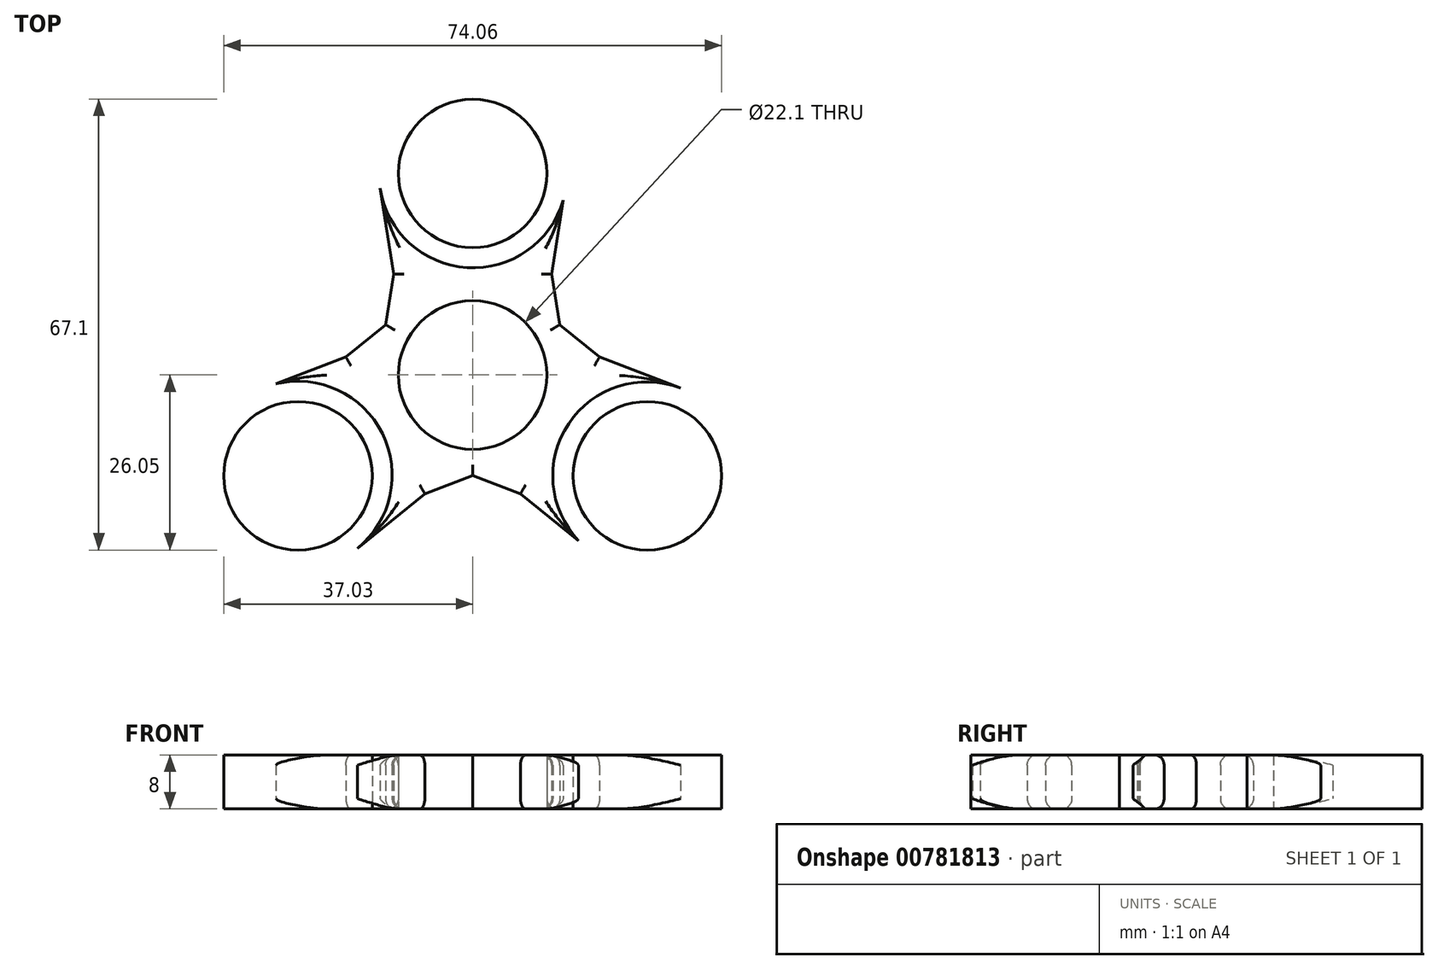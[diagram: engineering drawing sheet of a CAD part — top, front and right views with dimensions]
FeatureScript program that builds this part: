
annotation { "Feature Type Name" : "Feature", "Feature Type Description" : "" }
export const myFeature = defineFeature(function(context is Context, id is Id, definition is map)
    precondition{}
    {
        {
            var Q0;
            Q0=qCreatedBy(makeId("Top.planeOp"),FACE);
            var sketch = newSketch(context, id + "F0", { "sketchPlane" : qUnion([Q0])});
            skCircle(sketch, "E0", {"center": v(0, 0) * mm, "radius": 11.05 * mm});
            skCircle(sketch, "E1", {"center": v(0, 0) * mm, "radius": 14 * mm});
            skLineSegment(sketch, "E2", {"start": v(-20.51, 15) * mm, "end": v(20.51, 15) * mm, "construction": true});
            skLineSegment(sketch, "E3", {"start": v(0, 30) * mm, "end": v(0, 0) * mm, "construction": true});
            skSolve(sketch);
        }
        {
            var Q0;
            Q0=makeQuery(id+"F0.imprint","IMPRINT",FACE,{"disambiguationData":[TD([[makeQuery(id+"F0.imprint","IMPRINT",EDGE,{"derivedFrom":sQuery(id+"F0.wireOp",EDGE,"E0")}),-1.0]])]});
            extrude(context, id + "F1", {"entities" : qUnion([Q0]), "depth" : 8 * mm, "offsetDistance" : 25 * mm});
        }
        {
            var Q0;
            Q0=qCreatedBy(makeId("Top.planeOp"),FACE);
            var sketch = newSketch(context, id + "F2", { "sketchPlane" : qUnion([Q0])});
            skCircle(sketch, "E4.MirrorC", {"center": v(0.06, 29.96) * mm, "radius": 14 * mm});
            skCircle(sketch, "E5.MirrorC", {"center": v(0, 30) * mm, "radius": 11.05 * mm});
            skLineSegment(sketch, "E6.0", {"start": v(-20.51, 15) * mm, "end": v(20.51, 15) * mm, "construction": true});
            skLineSegment(sketch, "E7", {"start": v(-13.77, 27.77) * mm, "end": v(-11.75, 15) * mm});
            skCircle(sketch, "E8.0", {"center": v(0, 0) * mm, "radius": 14 * mm});
            skLineSegment(sketch, "E9", {"start": v(-11.75, 15) * mm, "end": v(-12.97, 7.49) * mm});
            skLineSegment(sketch, "E10.MirrorCS", {"start": v(13.77, 27.77) * mm, "end": v(11.75, 15) * mm});
            skLineSegment(sketch, "E11.MirrorCS", {"start": v(11.75, 15) * mm, "end": v(12.97, 7.49) * mm});
            skCircle(sketch, "E12.1.0", {"center": v(-25.98, -15) * mm, "radius": 11.05 * mm});
            skCircle(sketch, "E12.1.1", {"center": v(-25.97, -14.93) * mm, "radius": 14 * mm});
            skLineSegment(sketch, "E12.1.2", {"start": v(-17.16, -25.8) * mm, "end": v(-7.12, -17.67) * mm});
            skLineSegment(sketch, "E12.1.3", {"start": v(-7.12, -17.67) * mm, "end": v(0, -14.97) * mm});
            skLineSegment(sketch, "E12.1.4", {"start": v(-18.86, 2.67) * mm, "end": v(-12.97, 7.49) * mm});
            skLineSegment(sketch, "E12.1.5", {"start": v(-30.93, -1.96) * mm, "end": v(-18.86, 2.67) * mm});
            skCircle(sketch, "E12.2.0", {"center": v(25.98, -15) * mm, "radius": 11.05 * mm});
            skCircle(sketch, "E12.2.1", {"center": v(25.91, -15.03) * mm, "radius": 14 * mm});
            skLineSegment(sketch, "E12.2.2", {"start": v(30.93, -1.96) * mm, "end": v(18.86, 2.67) * mm});
            skLineSegment(sketch, "E12.2.3", {"start": v(18.86, 2.67) * mm, "end": v(12.97, 7.49) * mm});
            skLineSegment(sketch, "E12.2.4", {"start": v(7.12, -17.67) * mm, "end": v(0, -14.97) * mm});
            skLineSegment(sketch, "E12.2.5", {"start": v(17.16, -25.8) * mm, "end": v(7.12, -17.67) * mm});
            skPoint(sketch, "E13.orphan", {"position": v(-8.85, 10.84) * mm});
            skPoint(sketch, "E14.orphan", {"position": v(-13.82, 2.25) * mm});
            skPoint(sketch, "E15.orphan", {"position": v(4.96, -13.1) * mm});
            skPoint(sketch, "E16.orphan", {"position": v(-4.96, -13.1) * mm});
            skPoint(sketch, "E17.orphan", {"position": v(13.82, 2.25) * mm});
            skPoint(sketch, "E18.orphan", {"position": v(8.85, 10.84) * mm});
            skSolve(sketch);
        }
        {
            var Q0;
            Q0=makeQuery(id+"F2.imprint","IMPRINT",FACE,{"disambiguationData":[TD([[makeQuery(id+"F2.imprint","IMPRINT",EDGE,{"derivedFrom":sQuery(id+"F2.wireOp",EDGE,"E5.MirrorC")}),1.0]])]});
            var Q1;
            {var subQ9=sQuery(id+"F2.wireOp",EDGE,"E7");Q1=makeQuery(id+"F2.imprint","IMPRINT",FACE,{"disambiguationData":[TD([[makeQuery(id+"F2.imprint","IMPRINT",EDGE,{"derivedFrom":subQ9}),1.0]])]});}
            var Q2;
            Q2=makeQuery(id+"F2.imprint","IMPRINT",FACE,{"disambiguationData":[TD([[makeQuery(id+"F2.imprint","IMPRINT",EDGE,{"derivedFrom":sQuery(id+"F2.wireOp",EDGE,"E12.1.0")}),1.0]])]});
            var Q3;
            Q3=makeQuery(id+"F2.imprint","IMPRINT",FACE,{"disambiguationData":[TD([[makeQuery(id+"F2.imprint","IMPRINT",EDGE,{"derivedFrom":sQuery(id+"F2.wireOp",EDGE,"E12.2.0")}),1.0]])]});
            extrude(context, id + "F3", {"entities" : qUnion([Q0, Q1, Q2, Q3]), "operationType" : NewBodyOperationType.ADD, "depth" : 8 * mm, "offsetDistance" : 25 * mm});
        }
        {
            var Q0;
            Q0=makeQuery(id+"F3.boolean.opBoolean","MERGE",FACE,{"derivedFrom":[makeQuery(id+"F1.opExtrude","CAP_FACE",FACE,{"disambiguationData":[OSD([sQuery(id+"F0.wireOp",EDGE,"E0"),sQuery(id+"F0.wireOp",EDGE,"E1")])],"isStart":true}),makeQuery(id+"F3.opExtrude","CAP_FACE",FACE,{"disambiguationData":[OSD([sQuery(id+"F2.wireOp",EDGE,"E4.MirrorC"),sQuery(id+"F2.wireOp",EDGE,"E5.MirrorC"),sQuery(id+"F2.wireOp",EDGE,"E7"),sQuery(id+"F2.wireOp",EDGE,"E8.0"),sQuery(id+"F2.wireOp",EDGE,"E9"),sQuery(id+"F2.wireOp",EDGE,"E10.MirrorCS"),sQuery(id+"F2.wireOp",EDGE,"E11.MirrorCS"),sQuery(id+"F2.wireOp",EDGE,"E12.1.0"),sQuery(id+"F2.wireOp",EDGE,"E12.1.1"),sQuery(id+"F2.wireOp",EDGE,"E12.1.2"),sQuery(id+"F2.wireOp",EDGE,"E12.1.3"),sQuery(id+"F2.wireOp",EDGE,"E12.1.4"),sQuery(id+"F2.wireOp",EDGE,"E12.1.5"),sQuery(id+"F2.wireOp",EDGE,"E12.2.0"),sQuery(id+"F2.wireOp",EDGE,"E12.2.1"),sQuery(id+"F2.wireOp",EDGE,"E12.2.2"),sQuery(id+"F2.wireOp",EDGE,"E12.2.3"),sQuery(id+"F2.wireOp",EDGE,"E12.2.4"),sQuery(id+"F2.wireOp",EDGE,"E12.2.5")])],"isStart":true})]});
            var Q1;
            Q1=makeQuery(id+"F3.boolean.opBoolean","MERGE",FACE,{"derivedFrom":[makeQuery(id+"F1.opExtrude","CAP_FACE",FACE,{"disambiguationData":[OSD([sQuery(id+"F0.wireOp",EDGE,"E0"),sQuery(id+"F0.wireOp",EDGE,"E1")])],"isStart":false}),makeQuery(id+"F3.opExtrude","CAP_FACE",FACE,{"disambiguationData":[OSD([sQuery(id+"F2.wireOp",EDGE,"E4.MirrorC"),sQuery(id+"F2.wireOp",EDGE,"E5.MirrorC"),sQuery(id+"F2.wireOp",EDGE,"E7"),sQuery(id+"F2.wireOp",EDGE,"E8.0"),sQuery(id+"F2.wireOp",EDGE,"E9"),sQuery(id+"F2.wireOp",EDGE,"E10.MirrorCS"),sQuery(id+"F2.wireOp",EDGE,"E11.MirrorCS"),sQuery(id+"F2.wireOp",EDGE,"E12.1.0"),sQuery(id+"F2.wireOp",EDGE,"E12.1.1"),sQuery(id+"F2.wireOp",EDGE,"E12.1.2"),sQuery(id+"F2.wireOp",EDGE,"E12.1.3"),sQuery(id+"F2.wireOp",EDGE,"E12.1.4"),sQuery(id+"F2.wireOp",EDGE,"E12.1.5"),sQuery(id+"F2.wireOp",EDGE,"E12.2.0"),sQuery(id+"F2.wireOp",EDGE,"E12.2.1"),sQuery(id+"F2.wireOp",EDGE,"E12.2.2"),sQuery(id+"F2.wireOp",EDGE,"E12.2.3"),sQuery(id+"F2.wireOp",EDGE,"E12.2.4"),sQuery(id+"F2.wireOp",EDGE,"E12.2.5")])],"isStart":false})]});
            fillet(context, id + "F4", {"entities" : qUnion([Q0, Q1]), "radius" : 1.5 * mm, "tangentPropagation" : true, "allowEdgeOverflow" : false});
        }
    });
